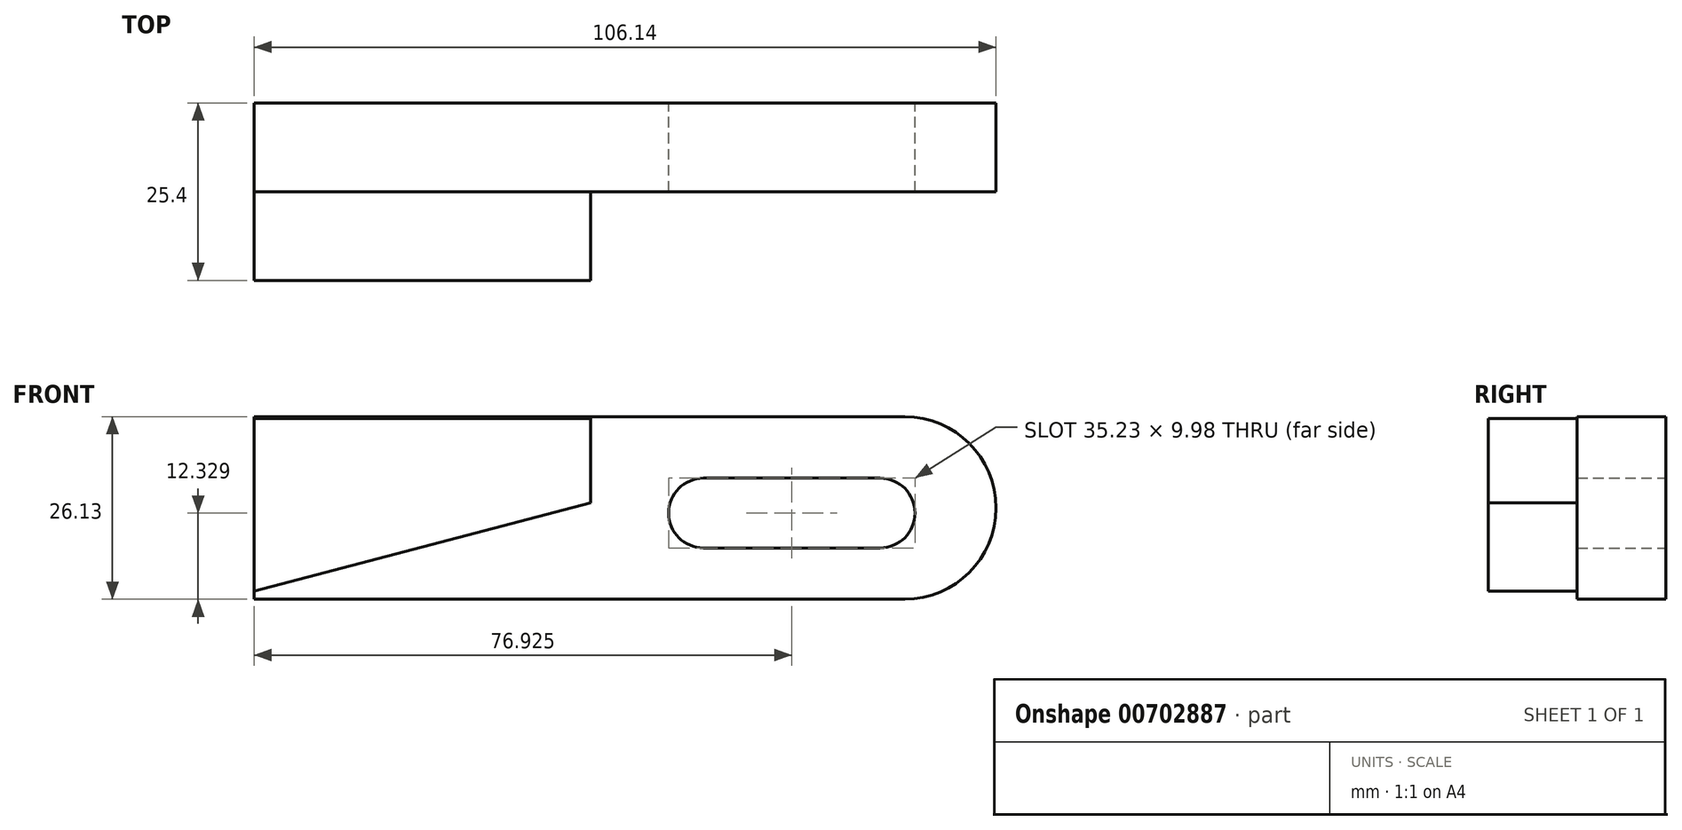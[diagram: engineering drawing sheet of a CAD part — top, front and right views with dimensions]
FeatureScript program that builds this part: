
annotation { "Feature Type Name" : "Feature", "Feature Type Description" : "" }
export const myFeature = defineFeature(function(context is Context, id is Id, definition is map)
    precondition{}
    {
        {
            var Q0;
            Q0=qCreatedBy(makeId("Front.planeOp"),FACE);
            var sketch = newSketch(context, id + "F0", { "sketchPlane" : qUnion([Q0])});
            skLineSegment(sketch, "E0", {"start": v(-57.4, 8.51) * mm, "end": v(-57.4, -16.15) * mm});
            skLineSegment(sketch, "E1", {"start": v(-57.4, -16.15) * mm, "end": v(-9.25, -3.52) * mm});
            skLineSegment(sketch, "E2", {"start": v(-9.25, -3.52) * mm, "end": v(-9.25, 8.51) * mm});
            skLineSegment(sketch, "E3", {"start": v(-9.25, 8.51) * mm, "end": v(-57.4, 8.51) * mm});
            skSolve(sketch);
        }
        {
            var Q0;
            Q0 = qSketchRegion(id + "F0", true);
            extrude(context, id + "F1", {"entities" : qUnion([Q0]), "depth" : 25.4 * mm, "offsetDistance" : 25.4 * mm});
        }
        {
            var Q0;
            Q0=qCreatedBy(makeId("Front.planeOp"),FACE);
            var sketch = newSketch(context, id + "F2", { "sketchPlane" : qUnion([Q0])});
            skLineSegment(sketch, "E4.bottom", {"start": v(-57.4, 8.8) * mm, "end": v(35.67, 8.8) * mm});
            skLineSegment(sketch, "E4.top", {"start": v(-57.4, -17.32) * mm, "end": v(35.67, -17.32) * mm});
            skLineSegment(sketch, "E4.left", {"start": v(-57.4, 8.8) * mm, "end": v(-57.4, -17.32) * mm});
            skArc(sketch, "E5", {"start": v(35.67, -17.32) * mm, "mid": v(48.74, -4.26) * mm, "end": v(35.67, 8.8) * mm});
            skLineSegment(sketch, "E6.bottom", {"start": v(6.9, 0) * mm, "end": v(32.15, 0) * mm});
            skLineSegment(sketch, "E6.top", {"start": v(6.9, -9.98) * mm, "end": v(32.15, -9.98) * mm});
            skArc(sketch, "E7", {"start": v(6.9, 0) * mm, "mid": v(1.9, -5) * mm, "end": v(6.9, -9.98) * mm});
            skArc(sketch, "E8", {"start": v(32.15, -9.98) * mm, "mid": v(37.14, -5) * mm, "end": v(32.15, 0) * mm});
            skSolve(sketch);
        }
        {
            var Q0;
            Q0 = qSketchRegion(id + "F2", true);
            extrude(context, id + "F3", {"entities" : qUnion([Q0]), "operationType" : NewBodyOperationType.ADD, "depth" : 12.7 * mm, "offsetDistance" : 25.4 * mm});
        }
    });
